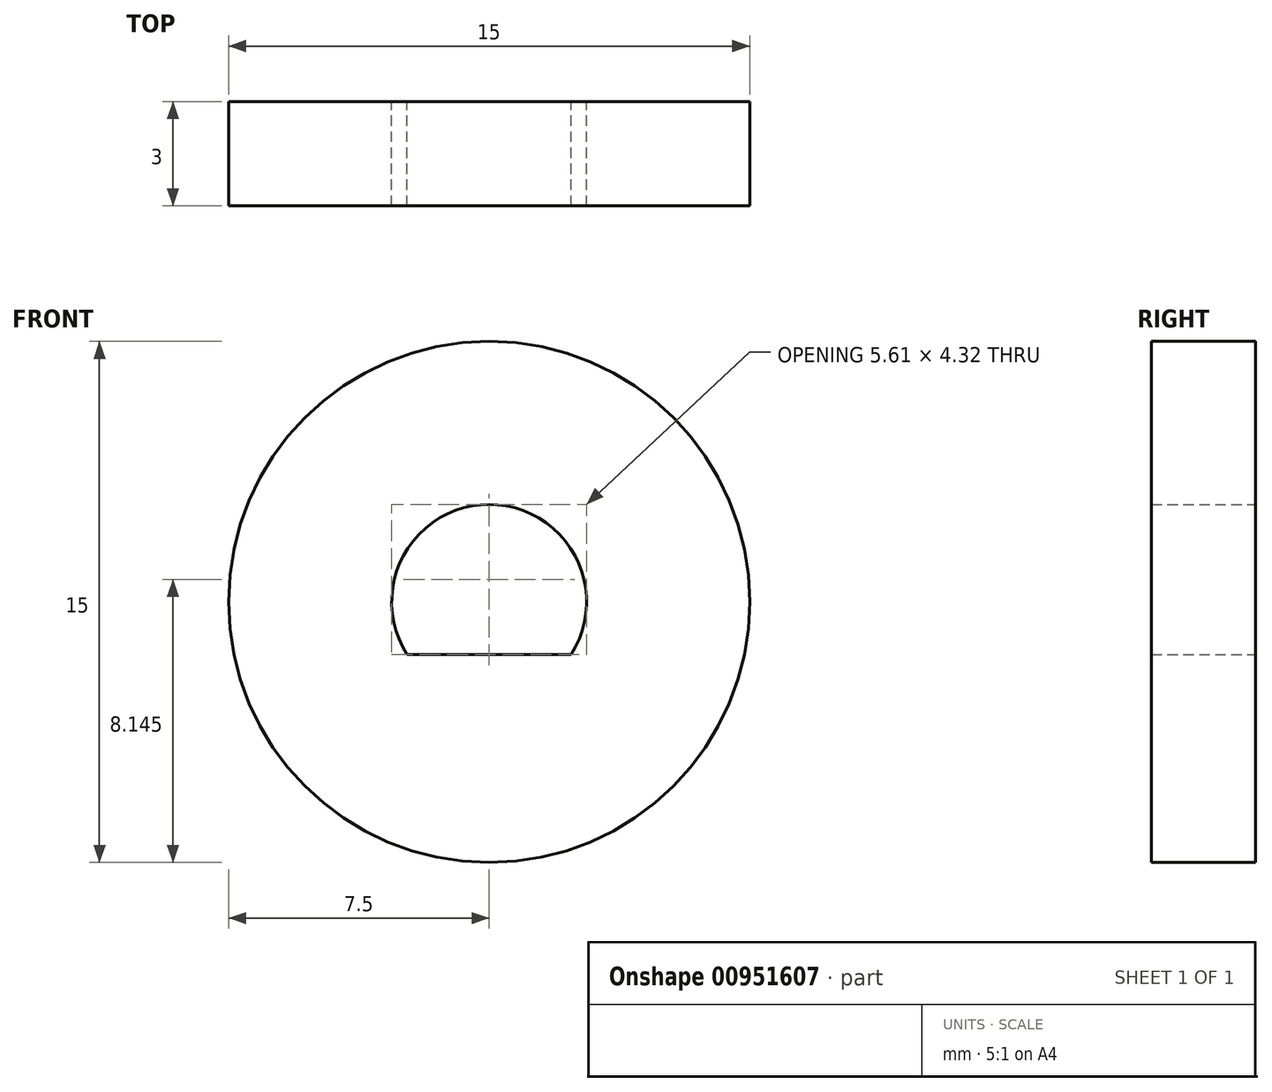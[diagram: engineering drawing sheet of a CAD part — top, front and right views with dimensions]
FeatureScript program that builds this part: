
annotation { "Feature Type Name" : "Feature", "Feature Type Description" : "" }
export const myFeature = defineFeature(function(context is Context, id is Id, definition is map)
    precondition{}
    {
        {
            var Q0;
            Q0=qCreatedBy(makeId("Front.planeOp"),FACE);
            var sketch = newSketch(context, id + "F0", { "sketchPlane" : qUnion([Q0])});
            skCircle(sketch, "E0", {"center": v(0, 0) * mm, "radius": 7.5 * mm});
            skLineSegment(sketch, "E1", {"start": v(0, 2.8) * mm, "end": v(0, -1.51) * mm, "construction": true});
            skLineSegment(sketch, "E2", {"start": v(0, -1.51) * mm, "end": v(2.36, -1.51) * mm});
            skLineSegment(sketch, "E3.MirrorCS", {"start": v(0, -1.51) * mm, "end": v(-2.36, -1.51) * mm});
            skArc(sketch, "E4", {"start": v(2.36, -1.51) * mm, "mid": v(0, 2.8) * mm, "end": v(-2.36, -1.51) * mm});
            skPoint(sketch, "E5", {"position": v(0, 2.8) * mm});
            skSolve(sketch);
        }
        {
            var Q0;
            Q0=qSketchRegion(id+"F0",true);
            extrude(context, id + "F1", {"entities" : qUnion([Q0]), "depth" : 3 * mm, "offsetDistance" : 25 * mm});
        }
    });
